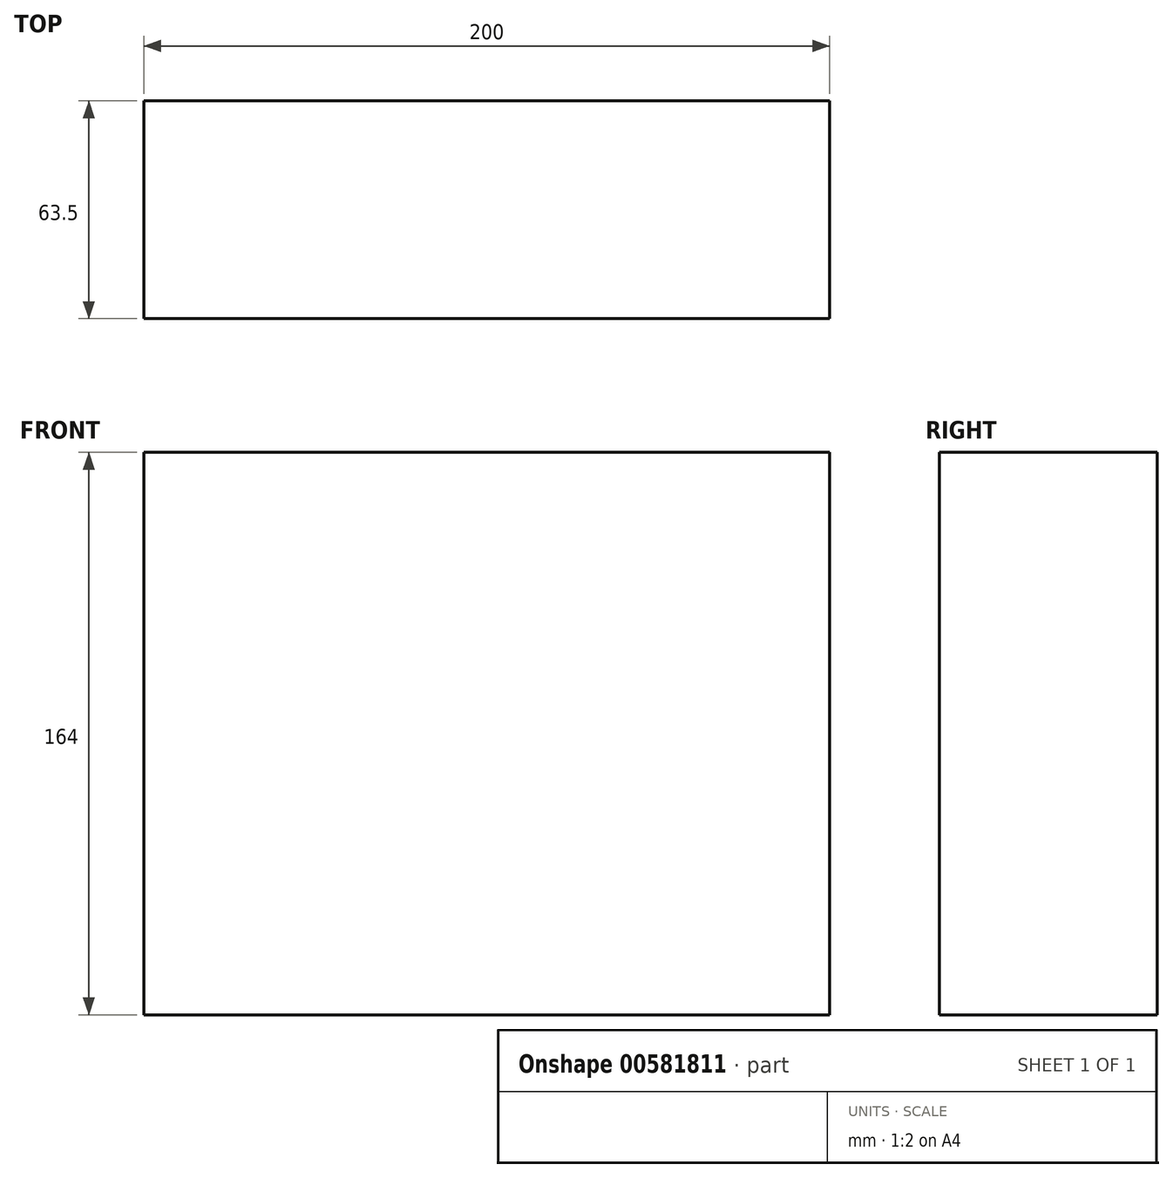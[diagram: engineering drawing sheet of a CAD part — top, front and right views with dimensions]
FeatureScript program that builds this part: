
annotation { "Feature Type Name" : "Feature", "Feature Type Description" : "" }
export const myFeature = defineFeature(function(context is Context, id is Id, definition is map)
    precondition{}
    {
        {
            var Q0;
            Q0=qCreatedBy(makeId("Front.planeOp"),FACE);
            var sketch = newSketch(context, id + "F0", { "sketchPlane" : qUnion([Q0])});
            skLineSegment(sketch, "E0.bottom", {"start": v(-100, 82) * mm, "end": v(100, 82) * mm});
            skLineSegment(sketch, "E0.top", {"start": v(-100, -82) * mm, "end": v(100, -82) * mm});
            skLineSegment(sketch, "E0.left", {"start": v(-100, 82) * mm, "end": v(-100, -82) * mm});
            skLineSegment(sketch, "E0.right", {"start": v(100, 82) * mm, "end": v(100, -82) * mm});
            skPoint(sketch, "E0.middle", {"position": v(0, 0) * mm});
            skSolve(sketch);
        }
        {
            var Q0;
            Q0 = qSketchRegion(id + "F0", true);
            extrude(context, id + "F1", {"entities" : qUnion([Q0]), "depth" : 63.5 * mm, "offsetDistance" : 25 * mm});
        }
        {
            var Q0;
            Q0 = qSketchRegion(id + "F0", true);
            extrude(context, id + "F2", {"entities" : qUnion([Q0]), "operationType" : NewBodyOperationType.ADD, "depth" : 62.5 * mm, "offsetDistance" : 25 * mm});
        }
    });
